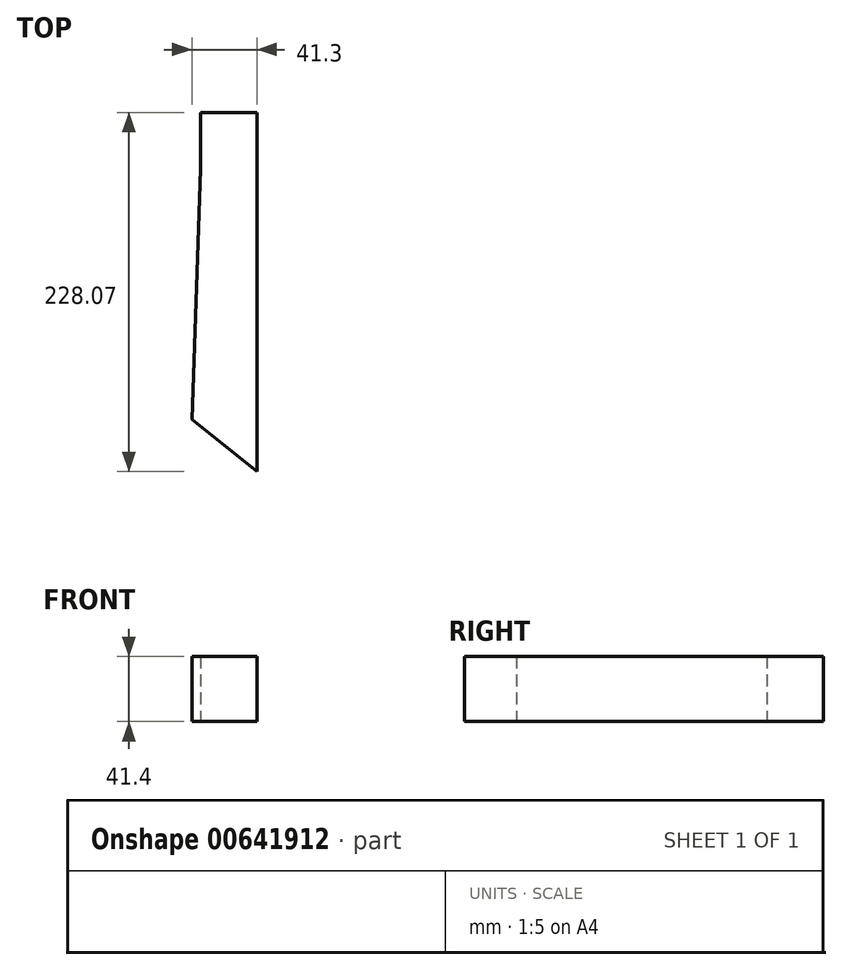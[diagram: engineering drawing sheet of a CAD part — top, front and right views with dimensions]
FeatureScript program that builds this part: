
annotation { "Feature Type Name" : "Feature", "Feature Type Description" : "" }
export const myFeature = defineFeature(function(context is Context, id is Id, definition is map)
    precondition{}
    {
        {
            var Q0;
            Q0=qCreatedBy(makeId("Top.planeOp"),FACE);
            var sketch = newSketch(context, id + "F0", { "sketchPlane" : qUnion([Q0])});
            skLineSegment(sketch, "E0", {"start": v(-113.44, -27.05) * mm, "end": v(-113.44, 9.09) * mm});
            skLineSegment(sketch, "E1", {"start": v(-113.44, 9.09) * mm, "end": v(-77.73, 9.09) * mm});
            skLineSegment(sketch, "E2", {"start": v(-77.73, 9.09) * mm, "end": v(-77.73, -139.99) * mm});
            skLineSegment(sketch, "E3", {"start": v(-77.73, -139.99) * mm, "end": v(-77.73, -218.98) * mm});
            skLineSegment(sketch, "E4", {"start": v(-113.44, -27.05) * mm, "end": v(-119.03, -185.94) * mm});
            skLineSegment(sketch, "E5", {"start": v(-119.03, -185.94) * mm, "end": v(-77.73, -218.98) * mm});
            skSolve(sketch);
        }
        {
            var Q0;
            Q0=makeQuery(id+"F0.imprint","IMPRINT",FACE,{"disambiguationData":[TD([[makeQuery(id+"F0.imprint","IMPRINT",EDGE,{"derivedFrom":sQuery(id+"F0.wireOp",EDGE,"E0")}),-1.0]])]});
            extrude(context, id + "F1", {"entities" : qUnion([Q0]), "depth" : 41.4 * mm, "offsetDistance" : 25.4 * mm});
        }
    });
